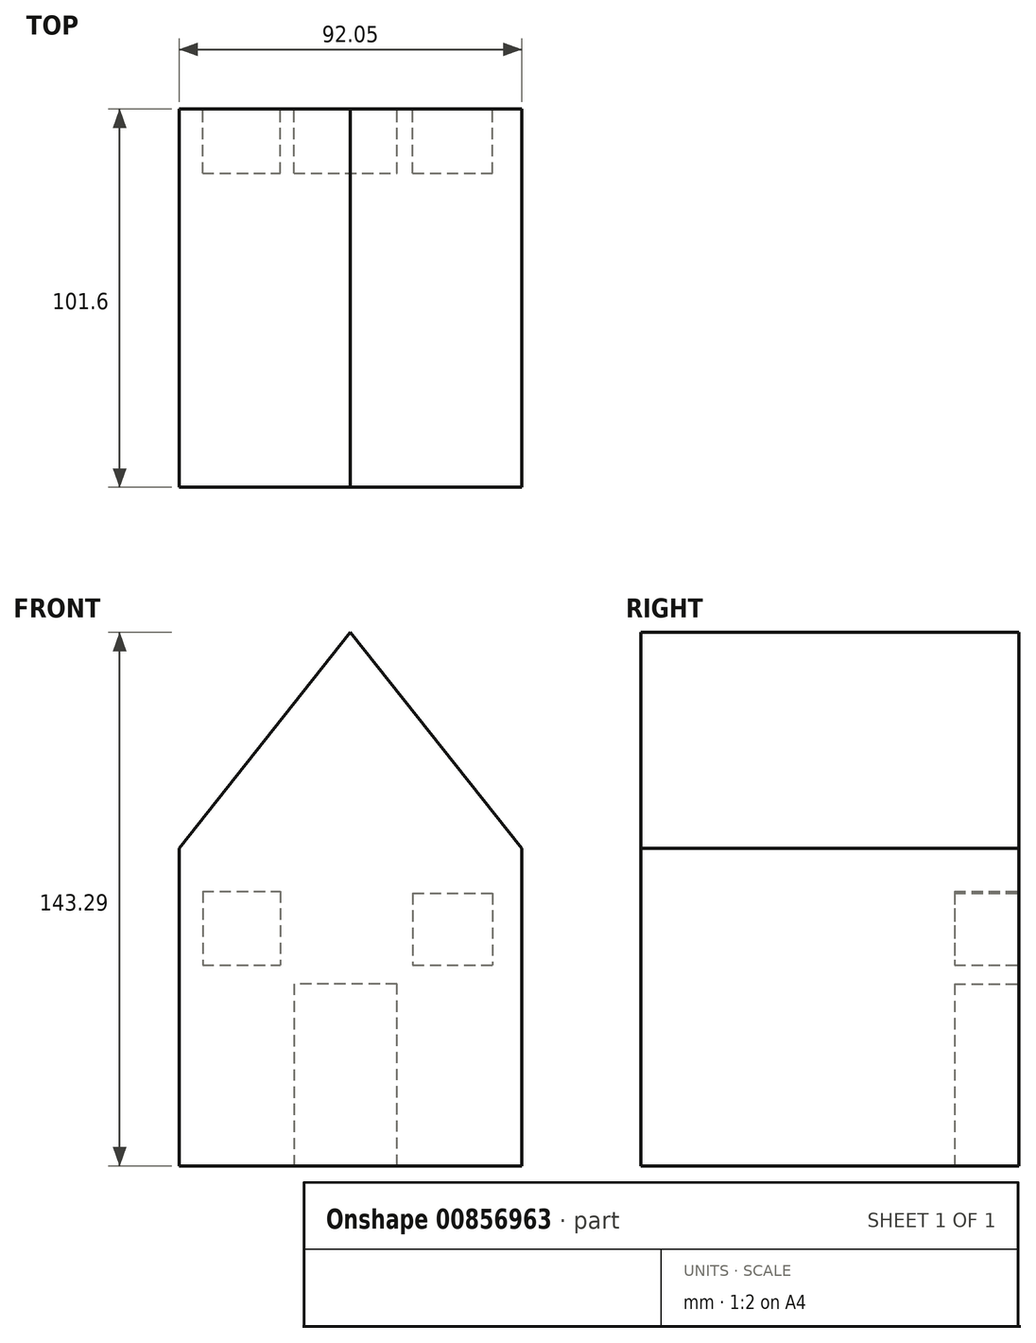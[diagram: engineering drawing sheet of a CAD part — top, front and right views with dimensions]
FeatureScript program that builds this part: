
annotation { "Feature Type Name" : "Feature", "Feature Type Description" : "" }
export const myFeature = defineFeature(function(context is Context, id is Id, definition is map)
    precondition{}
    {
        {
            var Q0;
            Q0=qCreatedBy(makeId("Front.planeOp"),FACE);
            var sketch = newSketch(context, id + "F0", { "sketchPlane" : qUnion([Q0])});
            skLineSegment(sketch, "E0.bottom", {"start": v(-44.72, 36.34) * mm, "end": v(47.33, 36.34) * mm});
            skLineSegment(sketch, "E0.top", {"start": v(-44.72, -48.9) * mm, "end": v(47.33, -48.9) * mm});
            skLineSegment(sketch, "E0.left", {"start": v(-44.72, 36.34) * mm, "end": v(-44.72, -48.9) * mm});
            skLineSegment(sketch, "E0.right", {"start": v(47.33, 36.34) * mm, "end": v(47.33, -48.9) * mm});
            skLineSegment(sketch, "E1", {"start": v(1.3, 94.4) * mm, "end": v(-44.72, 36.34) * mm});
            skPoint(sketch, "E1.startSnap0", {"position": v(1.3, 36.34) * mm});
            skLineSegment(sketch, "E2", {"start": v(1.3, 94.4) * mm, "end": v(47.33, 36.34) * mm});
            skSolve(sketch);
        }
        {
            var Q0;
            Q0=qCreatedBy(makeId("Front.planeOp"),FACE);
            var sketch = newSketch(context, id + "F1", { "sketchPlane" : qUnion([Q0])});
            skLineSegment(sketch, "E3.bottom", {"start": v(18.04, 24.32) * mm, "end": v(39.48, 24.32) * mm});
            skLineSegment(sketch, "E3.top", {"start": v(18.04, 4.97) * mm, "end": v(39.48, 4.97) * mm});
            skLineSegment(sketch, "E3.left", {"start": v(18.04, 24.32) * mm, "end": v(18.04, 4.97) * mm});
            skLineSegment(sketch, "E3.right", {"start": v(39.48, 24.32) * mm, "end": v(39.48, 4.97) * mm});
            skPoint(sketch, "E4.oppositeSnap0", {"position": v(28.76, 4.97) * mm});
            skLineSegment(sketch, "E4.bottom", {"start": v(-38.44, 24.84) * mm, "end": v(-17.52, 24.84) * mm});
            skLineSegment(sketch, "E4.top", {"start": v(-38.44, 4.97) * mm, "end": v(-17.52, 4.97) * mm});
            skLineSegment(sketch, "E4.left", {"start": v(-38.44, 24.84) * mm, "end": v(-38.44, 4.97) * mm});
            skLineSegment(sketch, "E4.right", {"start": v(-17.52, 24.84) * mm, "end": v(-17.52, 4.97) * mm});
            skLineSegment(sketch, "E5", {"start": v(-13.93, 0) * mm, "end": v(-13.93, -48.9) * mm});
            skLineSegment(sketch, "E6", {"start": v(-13.93, -48.9) * mm, "end": v(13.78, -48.9) * mm});
            skLineSegment(sketch, "E7", {"start": v(13.78, -48.9) * mm, "end": v(13.78, 0) * mm});
            skLineSegment(sketch, "E8", {"start": v(13.78, 0) * mm, "end": v(-13.93, 0) * mm});
            skSolve(sketch);
        }
        {
            var Q0;
            Q0 = qSketchRegion(id + "F0", true);
            extrude(context, id + "F2", {"entities" : qUnion([Q0]), "depth" : 101.6 * mm, "offsetDistance" : 25.4 * mm});
        }
        {
            var Q0;
            Q0 = qSketchRegion(id + "F1", true);
            extrude(context, id + "F3", {"entities" : qUnion([Q0]), "operationType" : NewBodyOperationType.REMOVE, "depth" : 17.27 * mm, "offsetDistance" : 25.4 * mm});
        }
    });
